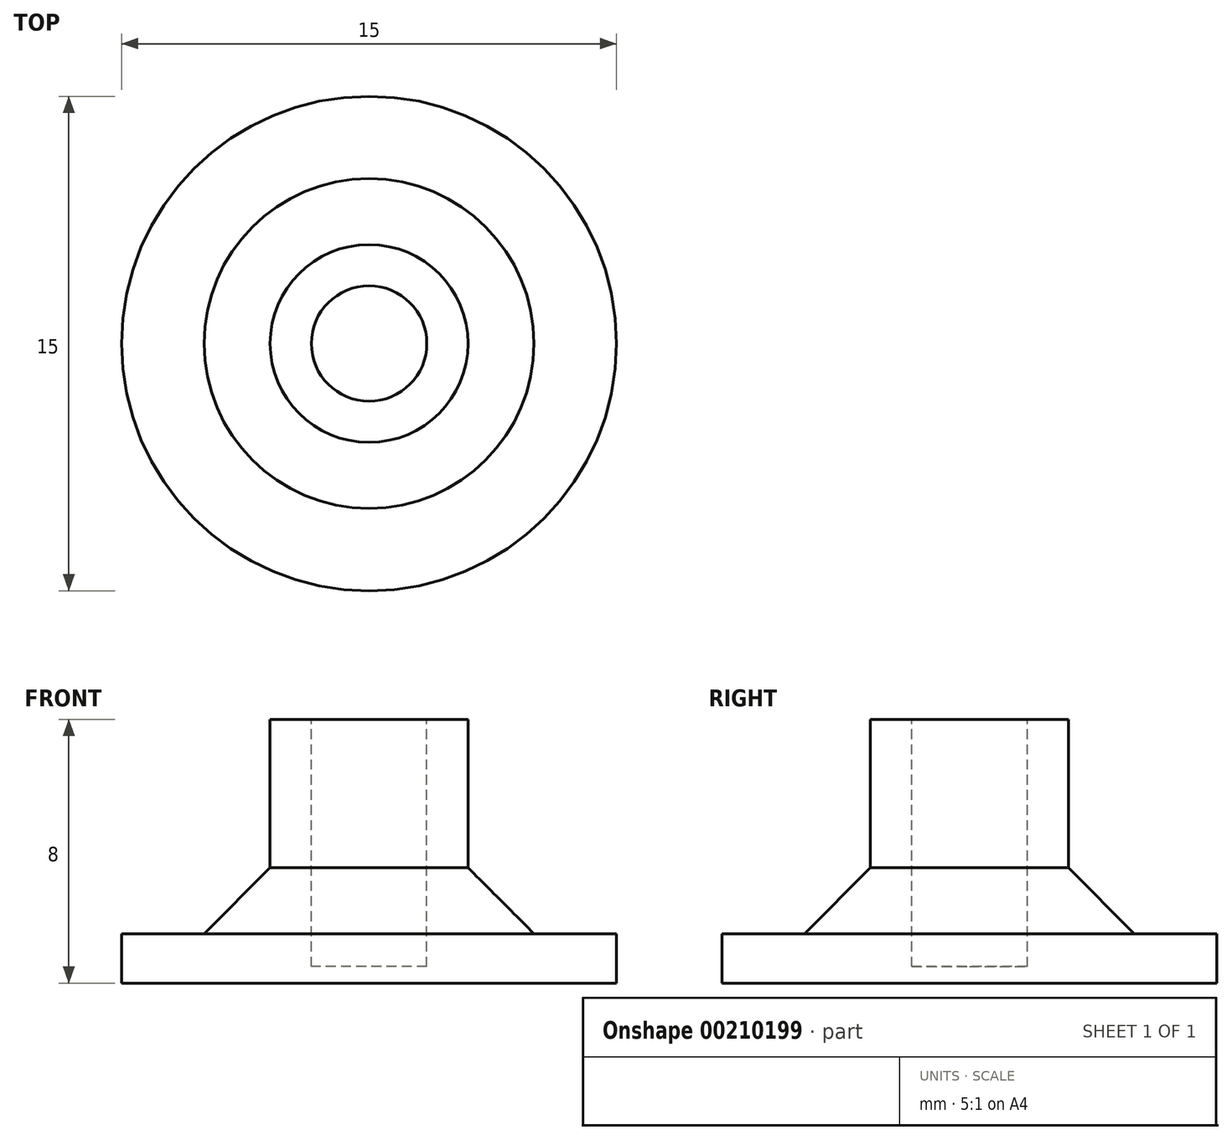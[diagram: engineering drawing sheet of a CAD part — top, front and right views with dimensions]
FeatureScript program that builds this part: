
annotation { "Feature Type Name" : "Feature", "Feature Type Description" : "" }
export const myFeature = defineFeature(function(context is Context, id is Id, definition is map)
    precondition{}
    {
        {
            var Q0;
            Q0=qCreatedBy(makeId("Front.planeOp"),FACE);
            var sketch = newSketch(context, id + "F0", { "sketchPlane" : qUnion([Q0])});
            skLineSegment(sketch, "E0", {"start": v(0, 0) * mm, "end": v(7.5, 0) * mm});
            skLineSegment(sketch, "E1", {"start": v(7.5, 0) * mm, "end": v(7.5, 1.5) * mm});
            skLineSegment(sketch, "E2", {"start": v(7.5, 1.5) * mm, "end": v(3, 1.5) * mm});
            skLineSegment(sketch, "E3", {"start": v(3, 1.5) * mm, "end": v(3, 8) * mm});
            skLineSegment(sketch, "E4", {"start": v(3, 8) * mm, "end": v(0, 8) * mm});
            skLineSegment(sketch, "E5", {"start": v(0, 8) * mm, "end": v(0, 0) * mm});
            skLineSegment(sketch, "E6", {"start": v(0, 6.86) * mm, "end": v(0, 8) * mm, "construction": true});
            skSolve(sketch);
        }
        {
            var Q0;
            Q0=makeQuery(id+"F0.imprint","IMPRINT",FACE,{"disambiguationData":[TD([[makeQuery(id+"F0.imprint","IMPRINT",EDGE,{"derivedFrom":sQuery(id+"F0.wireOp",EDGE,"E0")}),1.0]])]});
            var Q1;
            Q1=sQuery(id+"F0.wireOp",EDGE,"E6");
            revolve(context, id + "F1", {"entities" : qUnion([Q0]), "axis" : qUnion([Q1]), "revolveType" : RevolveType.FULL});
        }
        {
            var Q0;
            Q0=makeQuery(id+"F1.opRevolve","SWEPT_FACE",FACE,{"disambiguationData":[OSD([sQuery(id+"F0.wireOp",EDGE,"E4")])]});
            var sketch = newSketch(context, id + "F2", { "sketchPlane" : qUnion([Q0])});
            skCircle(sketch, "E7", {"center": v(0, 0) * mm, "radius": 1.75 * mm});
            skSolve(sketch);
        }
        {
            var Q0;
            Q0 = qSketchRegion(id + "F2", true);
            extrude(context, id + "F3", {"entities" : qUnion([Q0]), "operationType" : NewBodyOperationType.REMOVE, "oppositeDirection" : true, "depth" : 7.5 * mm});
        }
        {
            var Q0;
            Q0=makeQuery(id+"F1.opRevolve","SWEPT_EDGE",EDGE,{"disambiguationData":[OSD([sQuery(id+"F0.wireOp",EDGE,"E2"),sQuery(id+"F0.wireOp",EDGE,"E3")])]});
            chamfer(context, id + "F4", {"entities" : qUnion([Q0]), "width" : 2 * mm, "tangentPropagation" : true});
        }
    });
